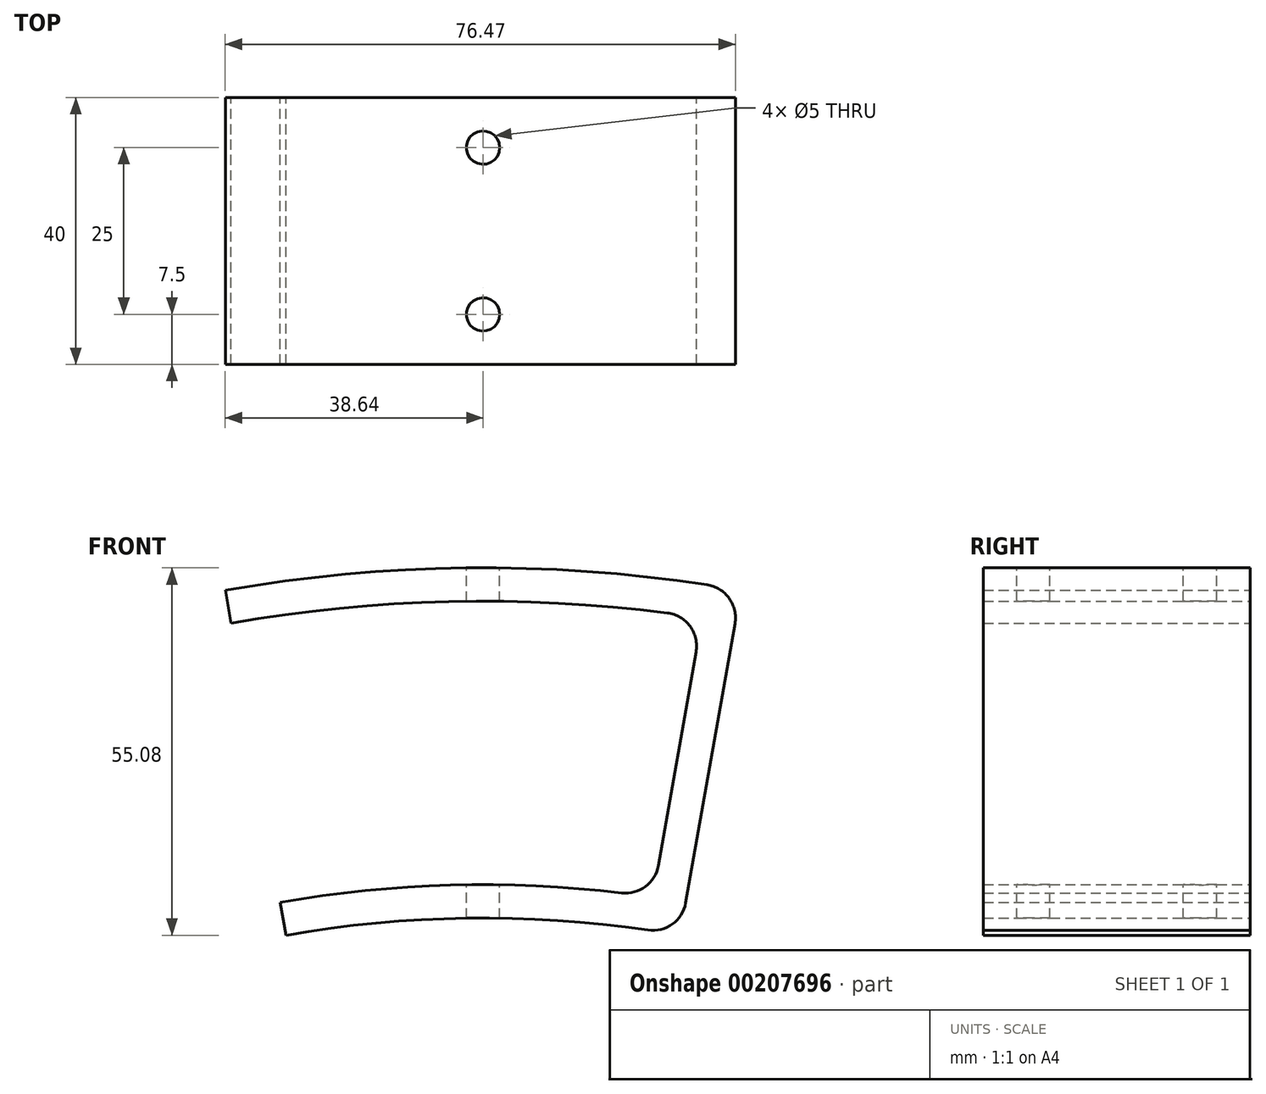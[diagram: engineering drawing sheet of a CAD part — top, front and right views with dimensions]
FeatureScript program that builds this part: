
annotation { "Feature Type Name" : "Feature", "Feature Type Description" : "" }
export const myFeature = defineFeature(function(context is Context, id is Id, definition is map)
    precondition{}
    {
        {
            var Q0;
            Q0=qCreatedBy(makeId("Front.planeOp"),FACE);
            var sketch = newSketch(context, id + "F0", { "sketchPlane" : qUnion([Q0])});
            skCircle(sketch, "E0", {"center": v(0, 0) * mm, "radius": 222.5 * mm});
            skLineSegment(sketch, "E1", {"start": v(-38.64, 219.12) * mm, "end": v(0, 0) * mm});
            skLineSegment(sketch, "E2", {"start": v(38.64, 219.12) * mm, "end": v(0, 0) * mm});
            skCircle(sketch, "E3", {"center": v(0, 0) * mm, "radius": 217.5 * mm});
            skLineSegment(sketch, "E4", {"start": v(32.83, 215) * mm, "end": v(25.45, 173.14) * mm});
            skCircle(sketch, "E5", {"center": v(0, 0) * mm, "radius": 170 * mm});
            skCircle(sketch, "E6", {"center": v(0, 0) * mm, "radius": 175 * mm});
            skSolve(sketch);
        }
        {
            var Q0;
            {var subQ1=sQuery(id+"F0.wireOp",EDGE,"E0");var subQ5=sQuery(id+"F0.wireOp",EDGE,"E1");var subQ6=makeQuery(id+"F0.imprint","INTERSECT",VERTEX,{"derivedFrom":[subQ1,subQ5]});Q0=makeQuery(id+"F0.imprint","IMPRINT",FACE,{"disambiguationData":[TD([[makeQuery(id+"F0.imprint","IMPRINT",EDGE,{"disambiguationData":[TD([[subQ6,1.0]])],"derivedFrom":subQ1}),1.0]])]});}
            var Q1;
            {var subQ5=sQuery(id+"F0.wireOp",EDGE,"E4");Q1=makeQuery(id+"F0.imprint","IMPRINT",FACE,{"disambiguationData":[TD([[makeQuery(id+"F0.imprint","IMPRINT",EDGE,{"derivedFrom":subQ5}),1.0]])]});}
            var Q2;
            {var subQ0=sQuery(id+"F0.wireOp",EDGE,"E6");var subQ6=sQuery(id+"F0.wireOp",EDGE,"E1");var subQ8=makeQuery(id+"F0.imprint","INTERSECT",VERTEX,{"derivedFrom":[subQ6,subQ0]});Q2=makeQuery(id+"F0.imprint","IMPRINT",FACE,{"disambiguationData":[TD([[makeQuery(id+"F0.imprint","IMPRINT",EDGE,{"disambiguationData":[TD([[subQ8,-1.0]])],"derivedFrom":subQ6}),1.0]])]});}
            extrude(context, id + "F1", {"entities" : qUnion([Q0, Q1, Q2]), "endBound" : BoundingType.SYMMETRIC, "depth" : 40 * mm});
        }
        {
            var Q0;
            Q0=makeQuery(id+"F1.opExtrude","SWEPT_EDGE",EDGE,{"disambiguationData":[OSD([sQuery(id+"F0.wireOp",EDGE,"E0"),sQuery(id+"F0.wireOp",EDGE,"E2")])]});
            var Q1;
            Q1=makeQuery(id+"F1.opExtrude","SWEPT_EDGE",EDGE,{"disambiguationData":[OSD([sQuery(id+"F0.wireOp",EDGE,"E3"),sQuery(id+"F0.wireOp",EDGE,"E4")])]});
            var Q2;
            Q2=makeQuery(id+"F1.opExtrude","SWEPT_EDGE",EDGE,{"disambiguationData":[OSD([sQuery(id+"F0.wireOp",EDGE,"E2"),sQuery(id+"F0.wireOp",EDGE,"E5")])]});
            var Q3;
            Q3=makeQuery(id+"F1.opExtrude","SWEPT_EDGE",EDGE,{"disambiguationData":[OSD([sQuery(id+"F0.wireOp",EDGE,"E4"),sQuery(id+"F0.wireOp",EDGE,"E6")])]});
            fillet(context, id + "F2", {"entities" : qUnion([Q0, Q1, Q2, Q3]), "radius" : 5 * mm, "tangentPropagation" : true, "allowEdgeOverflow" : false});
        }
        {
            var Q0;
            Q0=qCreatedBy(makeId("Top.planeOp"),FACE);
            cPlane(context, id + "F3", {"entities" : qUnion([Q0]), "cplaneType" : CPlaneType.OFFSET, "offset" : 230 * mm, "width" : 150 * mm, "height" : 150 * mm});
        }
        {
            var Q0;
            Q0=qCreatedBy(id+"F3.planeOp",FACE);
            var sketch = newSketch(context, id + "F4", { "sketchPlane" : qUnion([Q0])});
            skCircle(sketch, "E7", {"center": v(0, 12.5) * mm, "radius": 2.5 * mm});
            skCircle(sketch, "E8", {"center": v(0, -12.5) * mm, "radius": 2.5 * mm});
            skSolve(sketch);
        }
        {
            var Q0;
            Q0 = qSketchRegion(id + "F4", true);
            extrude(context, id + "F5", {"entities" : qUnion([Q0]), "operationType" : NewBodyOperationType.REMOVE, "endBound" : BoundingType.THROUGH_ALL, "oppositeDirection" : true, "depth" : 25 * mm});
        }
    });
